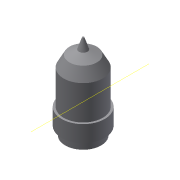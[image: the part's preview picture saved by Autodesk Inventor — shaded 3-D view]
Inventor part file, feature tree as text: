
AUTODESK INVENTOR PART (.ipt)
format: ipt  version: 2019.4 (Build 234330000, 330)  size: 116,224 bytes
history: native  units: mm
features: revolve x1, plane x1, sketch x1
ambient origin geometry x8: Origin, YZ Plane, XZ Plane, XY Plane, X Axis, Y Axis, Z Axis, Center Point
bodies: Solid1 (feature_tree)
feature tree (3):
  revolve  "Revolution1"  [1 undecoded]
  plane  "Work Plane1"
  sketch  "Sketch1"  dims[d0=43.1mm d1=10.125mm d2=4.67mm d3=2.025mm d4=90.0deg d5=9.27mm d7=7.73mm d8=39.36mm d9=90.0deg d10=19.21mm d11=11.0mm]
note: 1 required parameter value undecoded (feature->parameter linkage not recoverable at this tier; creation-order binding heuristic only, values carry confidence <= 0.55)
